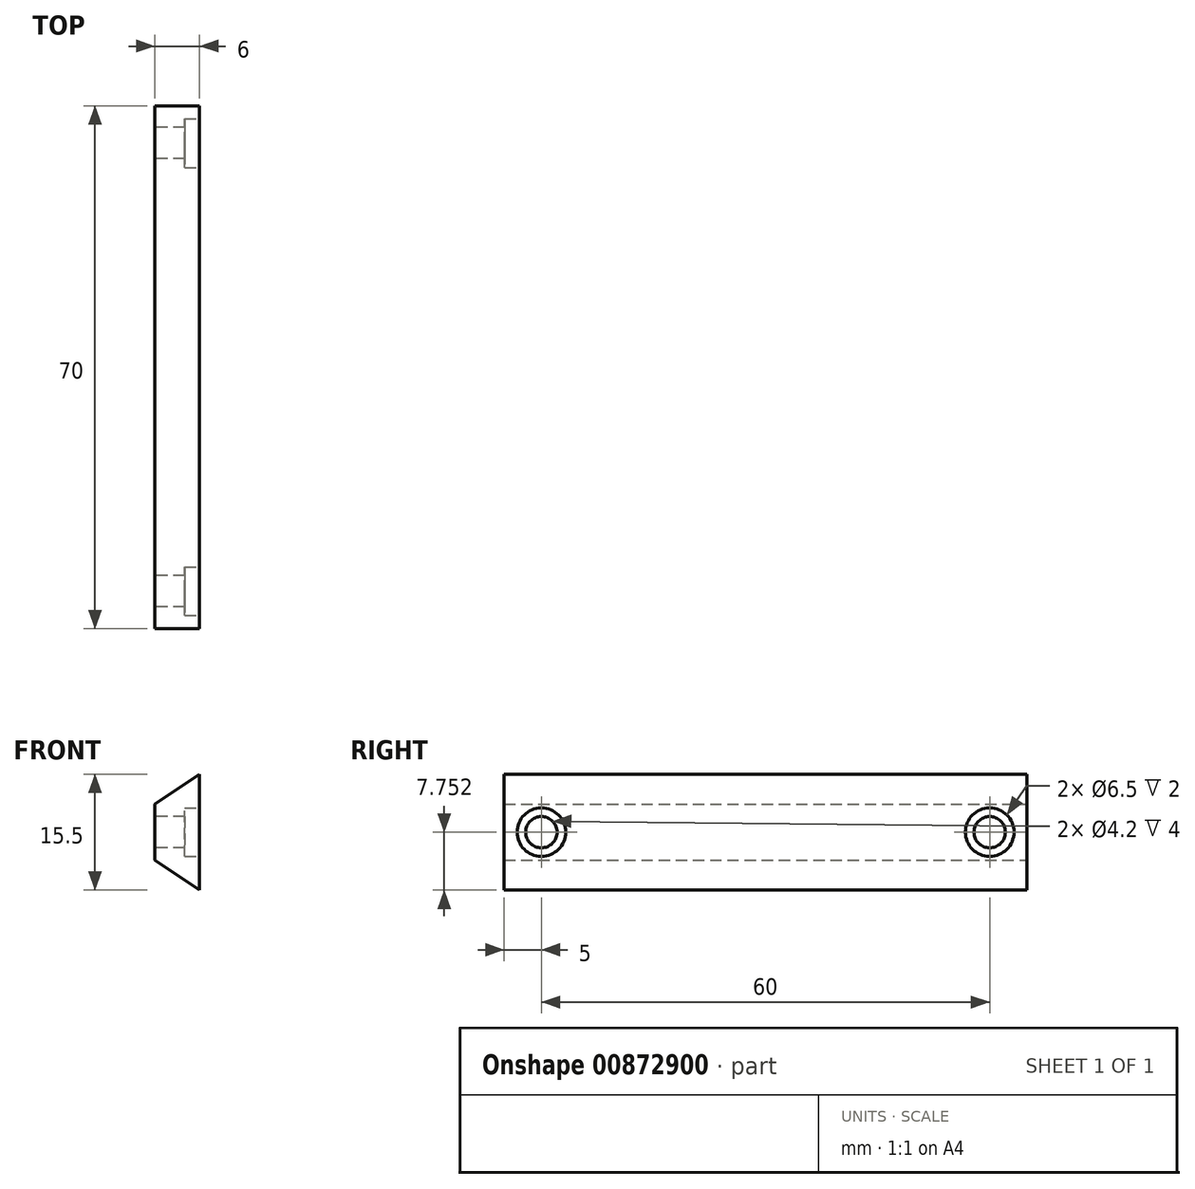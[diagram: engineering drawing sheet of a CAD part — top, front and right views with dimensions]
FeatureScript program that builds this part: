
annotation { "Feature Type Name" : "Feature", "Feature Type Description" : "" }
export const myFeature = defineFeature(function(context is Context, id is Id, definition is map)
    precondition{}
    {
        {
            var Q0;
            Q0=qCreatedBy(makeId("Front.planeOp"),FACE);
            var sketch = newSketch(context, id + "F0", { "sketchPlane" : qUnion([Q0])});
            skLineSegment(sketch, "E0", {"start": v(49.42, 27.74) * mm, "end": v(49.42, 12.24) * mm});
            skLineSegment(sketch, "E1", {"start": v(49.42, 12.24) * mm, "end": v(43.42, 16.24) * mm});
            skLineSegment(sketch, "E2", {"start": v(43.42, 16.24) * mm, "end": v(43.42, 23.74) * mm});
            skLineSegment(sketch, "E3", {"start": v(43.42, 23.74) * mm, "end": v(49.42, 27.74) * mm});
            skSolve(sketch);
        }
        {
            var Q0;
            Q0 = qSketchRegion(id + "F0", true);
            extrude(context, id + "F1", {"entities" : qUnion([Q0]), "depth" : 70 * mm, "offsetDistance" : 25 * mm});
        }
        {
            var Q0;
            Q0=makeQuery(id+"F1.opExtrude","SWEPT_FACE",FACE,{"disambiguationData":[OSD([sQuery(id+"F0.wireOp",EDGE,"E0")])]});
            var sketch = newSketch(context, id + "F2", { "sketchPlane" : qUnion([Q0])});
            skCircle(sketch, "E4", {"center": v(-65, 20) * mm, "radius": 3.25 * mm});
            skPoint(sketch, "E4.centerSnap0", {"position": v(-70, 20) * mm});
            skCircle(sketch, "E5", {"center": v(-5, 20) * mm, "radius": 3.25 * mm});
            skSolve(sketch);
        }
        {
            var Q0;
            Q0 = qSketchRegion(id + "F2", true);
            extrude(context, id + "F3", {"entities" : qUnion([Q0]), "operationType" : NewBodyOperationType.REMOVE, "oppositeDirection" : true, "depth" : 2 * mm, "offsetDistance" : 25 * mm});
        }
        {
            var Q0;
            Q0=makeQuery(id+"F1.opExtrude","SWEPT_FACE",FACE,{"disambiguationData":[OSD([sQuery(id+"F0.wireOp",EDGE,"E2")])]});
            var sketch = newSketch(context, id + "F4", { "sketchPlane" : qUnion([Q0])});
            skCircle(sketch, "E6", {"center": v(5, 20) * mm, "radius": 2.1 * mm});
            skPoint(sketch, "E6.centerSnap0", {"position": v(0, 20) * mm});
            skCircle(sketch, "E7", {"center": v(65, 20) * mm, "radius": 2.1 * mm});
            skSolve(sketch);
        }
        {
            var Q0;
            Q0 = qSketchRegion(id + "F4", true);
            extrude(context, id + "F5", {"entities" : qUnion([Q0]), "operationType" : NewBodyOperationType.REMOVE, "oppositeDirection" : true, "depth" : 4 * mm, "offsetDistance" : 25 * mm});
        }
    });
